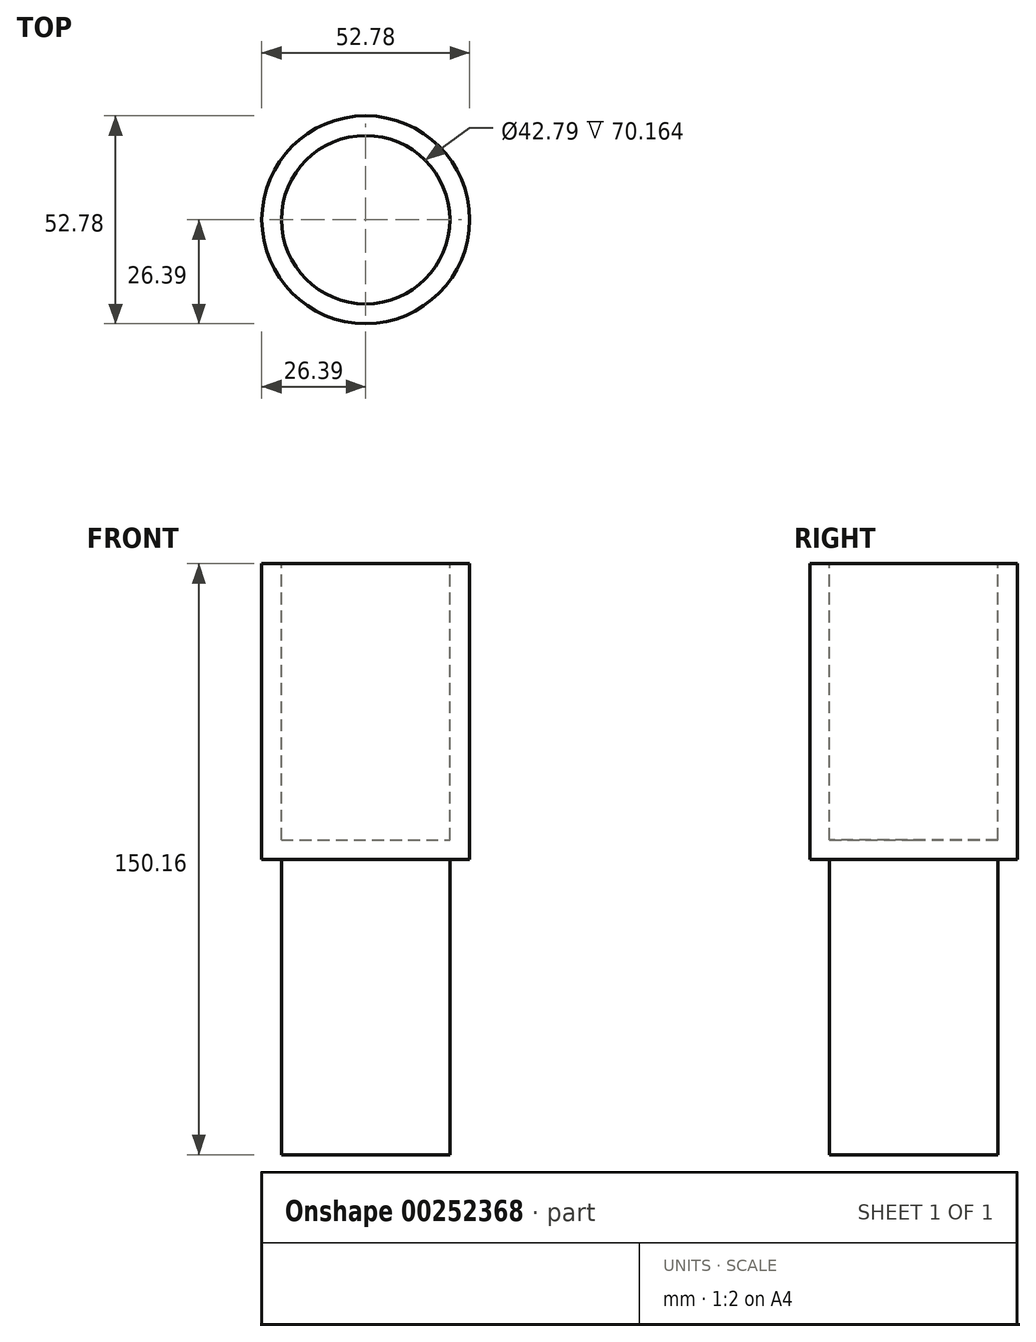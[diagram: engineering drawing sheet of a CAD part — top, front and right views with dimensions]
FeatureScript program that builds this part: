
annotation { "Feature Type Name" : "Feature", "Feature Type Description" : "" }
export const myFeature = defineFeature(function(context is Context, id is Id, definition is map)
    precondition{}
    {
        {
            var Q0;
            Q0=qCreatedBy(makeId("Front.planeOp"),FACE);
            var sketch = newSketch(context, id + "F0", { "sketchPlane" : qUnion([Q0])});
            skLineSegment(sketch, "E0.bottom", {"start": v(-26.4, 30.55) * mm, "end": v(28.69, 30.55) * mm});
            skLineSegment(sketch, "E0.top", {"start": v(-26.4, -44.61) * mm, "end": v(28.69, -44.61) * mm});
            skLineSegment(sketch, "E0.left", {"start": v(-26.4, 30.55) * mm, "end": v(-26.4, -44.61) * mm});
            skLineSegment(sketch, "E0.right", {"start": v(28.69, 30.55) * mm, "end": v(28.69, -44.61) * mm});
            skLineSegment(sketch, "E1", {"start": v(0, 30.55) * mm, "end": v(0, -44.61) * mm});
            skPoint(sketch, "E1.startSnap0", {"position": v(1.15, 30.55) * mm});
            skSolve(sketch);
        }
        {
            var Q0;
            {var subQ0=sQuery(id+"F0.wireOp",EDGE,"E0.left");Q0=makeQuery(id+"F0.imprint","IMPRINT",FACE,{"disambiguationData":[TD([[makeQuery(id+"F0.imprint","IMPRINT",EDGE,{"derivedFrom":subQ0}),1.0]])]});}
            var Q1;
            Q1=sQuery(id+"F0.wireOp",EDGE,"E1");
            revolve(context, id + "F1", {"entities" : qUnion([Q0]), "axis" : qUnion([Q1]), "revolveType" : RevolveType.FULL});
        }
        {
            var Q0;
            Q0=makeQuery(id+"F1.opRevolve","SWEPT_FACE",FACE,{"disambiguationData":[OSD([sQuery(id+"F0.wireOp",EDGE,"E0.bottom")])]});
            shell(context, id + "F2", {"entities" : qUnion([Q0]), "thickness" : 5 * mm});
        }
        {
            var Q0;
            Q0=makeQuery(id+"F2.opShell","OFFSET_FACE",FACE,{"disambiguationData":[OSD([sQuery(id+"F0.wireOp",EDGE,"E0.top")])]});
            extrude(context, id + "F3", {"entities" : qUnion([Q0]), "operationType" : NewBodyOperationType.ADD, "oppositeDirection" : true, "depth" : 80 * mm});
        }
    });
